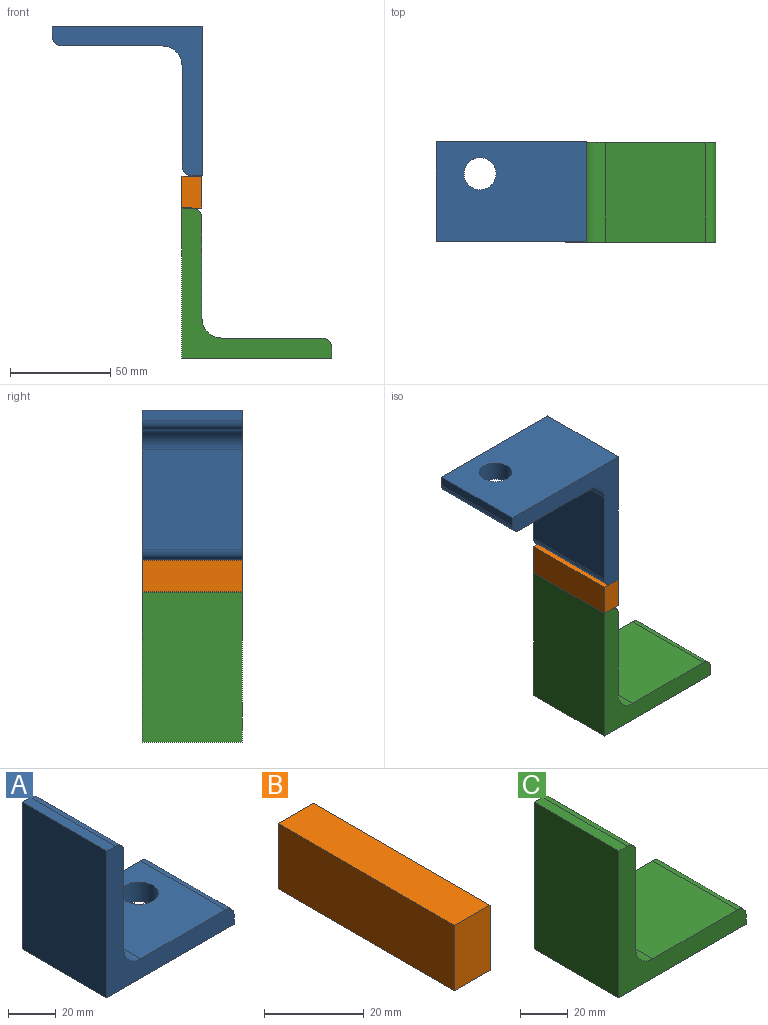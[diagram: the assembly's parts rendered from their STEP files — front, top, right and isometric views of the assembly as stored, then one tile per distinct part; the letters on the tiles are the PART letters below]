
ASSEMBLY  parts=3 mates=2
PART A: 12 faces, bbox 75x50x75 mm
  f0: plane 50x5mm, normal (0,0,1), area 250mm2, adj f1,f8,f9,f10
  f1: plane 75x50mm, normal (-1,0,0), area 3750mm2, adj f0,f2,f9,f10
  f2: plane 75x50mm, normal (0,0,-1), area 3548.9mm2, adj f1,f3,f9,f10,f11
  f3: plane 50x5mm, normal (1,0,0), area 250mm2, adj f2,f4,f9,f10
  f4: cylinder r=5mm len=50mm, axis (0,-1,0), area 392.7mm2, adj f3,f5,f9,f10
  f5: plane 50x50mm, normal (0,0,1), area 2298.9mm2, adj f4,f6,f9,f10,f11
  f6: cylinder r=10mm len=50mm, axis (0,-1,0), area 785.4mm2, adj f5,f7,f9,f10
  f7: plane 50x50mm, normal (1,0,0), area 2500mm2, adj f6,f8,f9,f10
  f8: cylinder r=5mm len=50mm, axis (0,-1,0), area 392.7mm2, adj f0,f7,f9,f10
  f9: plane 75x75mm, normal (0,1,0), area 1410.7mm2, adj f0,f1,f2,f3,f4,f5,f6,f7
  f10: plane 75x75mm, normal (0,-1,0), area 1410.7mm2, adj f0,f1,f2,f3,f4,f5,f6,f7
  f11: cylinder r=8mm len=16mm, axis (0,0,-1), area 502.7mm2, adj f2,f5
PART B: 6 faces, bbox 10x50x16 mm
  f0: plane 50x16mm, normal (-1,0,0), area 800mm2, adj f1,f3,f4,f5
  f1: plane 50x10mm, normal (0,0,-1), area 500mm2, adj f0,f2,f4,f5
  f2: plane 50x16mm, normal (1,0,0), area 800mm2, adj f1,f3,f4,f5
  f3: plane 50x10mm, normal (0,0,1), area 500mm2, adj f0,f2,f4,f5
  f4: plane 16x10mm, normal (0,1,0), area 160mm2, adj f0,f1,f2,f3
  f5: plane 16x10mm, normal (0,-1,0), area 160mm2, adj f0,f1,f2,f3
PART C: 11 faces, bbox 75x50x75 mm
  f0: plane 50x5mm, normal (0,0,1), area 250mm2, adj f1,f8,f9,f10
  f1: plane 75x50mm, normal (-1,0,0), area 3750mm2, adj f0,f2,f9,f10
  f2: plane 75x50mm, normal (0,0,-1), area 3750mm2, adj f1,f3,f9,f10
  f3: plane 50x5mm, normal (1,0,0), area 250mm2, adj f2,f4,f9,f10
  f4: cylinder r=5mm len=50mm, axis (0,-1,0), area 392.7mm2, adj f3,f5,f9,f10
  f5: plane 50x50mm, normal (0,0,1), area 2500mm2, adj f4,f6,f9,f10
  f6: cylinder r=10mm len=50mm, axis (0,-1,0), area 785.4mm2, adj f5,f7,f9,f10
  f7: plane 50x50mm, normal (1,0,0), area 2500mm2, adj f6,f8,f9,f10
  f8: cylinder r=5mm len=50mm, axis (0,-1,0), area 392.7mm2, adj f0,f7,f9,f10
  f9: plane 75x75mm, normal (0,1,0), area 1410.7mm2, adj f0,f1,f2,f3,f4,f5,f6,f7
  f10: plane 75x75mm, normal (0,-1,0), area 1410.7mm2, adj f0,f1,f2,f3,f4,f5,f6,f7
PLACE A rot(axis=(0,1,0),180deg) t=(-81.24,0,166)mm
PLACE B rot(axis=(0,1,0),0deg) t=(34.31,0,110.46)mm
PLACE C at identity fixed
MATE fastened A.f10 <-> C.f10  axis (0,-1,0) through (5,0,91)mm
MATE fastened A.f10 <-> B.f5  axis (0,-1,0) through (10,0,91)mm
